# Revit family: Systemtrenner Nachfüll 0305
name_source: partatom
category: Rohrzubehör
units: mm (PartAtom-declared; Revit-internal decimal feet)

## family parameters
Arbeitsebenenbasiert = Nein
Beim Laden mit Abzugskörper schneiden = Nein
Bemaßung runder Anschluss = Durchmesser verwenden
Gemeinsam genutzt = Nein
Immer vertikal = Ja
OmniClass-Nummer = 23.65.55.14
OmniClass-Titel = Valves for Liquid Services
Teiletyp = Unterbricht

## types (1)
- Systemtrenner Nachfüll 0305
    Anwendung = Systemtrenner haben gemäß EN 1717 die Aufgabe ein Rückdrücken, Rückfließen oder Rücksaugen von verschmutztem Wasser in das Trinkwassernetz zu verhindern.
Der Einsatzbereich ist überall dort wo eine Verbindung zwischen dem Trinkwassernetz und Nutzwasser durch feste oder flexible Leitungen hergestellt wird.
Bevorzugte Anwendungsgebiete sind Enthärtungs-, Entsäuerungs- und Entkarbonisierungsanlagen.
Außerdem können die Systemtrenner in Desinfektionsanlagen oder vor chemischen Reinigungsapparaten eingesetzt werden um das Rückfließen von chemisch belastetem Wasser zu verhindern.
    Ausgangsdruck (regelbar) = 0.5-3 bar
    D02 = 15.2 mm
    D03 = 14.4 mm  [stored 0.0472441 ft]
    D04 = 12.9 mm
    D05 = 10.6 mm  [stored 0.0347769 ft]
    D06 = 16 mm  [stored 0.0524934 ft]
    D07 = 22 mm  [stored 0.0721785 ft]
    D08 = 18 mm  [stored 0.0590551 ft]
    D09 = 13.5 mm
    D10 = 16.3 mm  [stored 0.0534777 ft]
    D11 = 23.7 mm  [stored 0.0777559 ft]
    D12 = 22.8 mm  [stored 0.0748031 ft]
    D13 = 19.2 mm
    D14 = 14.2 mm  [stored 0.0465879 ft]
    D15 = 12.2 mm
    D16 = 66.7 mm
    D17 = 66.5 mm
    D18 = 92.3 mm
    Dichtungen = EPDM entsprechend KTW
    Einbaulage = waagerecht
    Gehäuse = Messing, CW617N
    Hersteller = HERZ Armaturen Ges.m.b.H.
    Hinweis = Gemäß Art 33 der REACH-Verordnung (EG Nr. 1907/2006) sind wir verpflichtet, darauf hinzuweisen, dass der Stoff Blei auf der SVHC-Liste geführt wird und dass alle aus Messing bestehenden Bauteile, die in unseren Erzeugnissen verarbeitet sind, mehr als 0,1 % (w/w) Blei (CAS: 7439-92-1 / EINECS: 231-100-4) enthalten.
Da Blei als Legierungsbestandteil fest gebunden ist, sind keine Expositionen zu erwarten und daher sind keine zusätzlichen Angaben zur sicheren Verwendung notwendig.
    L03 = 13 mm
    L04 = 10 mm  [stored 0.0328084 ft]
    L05 = 4.8 mm  [stored 0.015748 ft]
    L08 = 15.5 mm
    L09 = 26.2 mm
    L10 = 23.3 mm
    L11 = 4 mm  [stored 0.0131234 ft]
    L12 = 4.8 mm  [stored 0.015748 ft]
    L13 = 8.7 mm
    L14 = 30 mm  [stored 0.0984252 ft]
    L15 = 18.8 mm
    L16 = 70.5 mm
    L17 = 6.5 mm
    L18 = 8.7 mm
    L19 = 36.7 mm
    L20 = 12 mm  [stored 0.0393701 ft]
    L21 = 11 mm  [stored 0.0360892 ft]
    L22 = 22 mm  [stored 0.0721785 ft]
    L23 = 34 mm  [stored 0.111549 ft]
    L24 = 10.1 mm
    L25 = 28.6 mm
    L26 = 48.5 mm
    L27 = 44.5 mm
    L28 = 85.3 mm
    L29 = 28.8 mm  [stored 0.0944882 ft]
    Max. Betriebsdruck = 1000000.0 Pa
    Max. Betriebstemperatur = 65 °C
    Max. Betriebstemperatur (Kurzzeitig) = 85 °C
    Medium = Wasser
    R01 = 8 mm  [stored 0.0262467 ft]
    R02 = 7 mm  [stored 0.0229659 ft]
    R03 = 8.5 mm  [stored 0.0278871 ft]
    R04 = 7.5 mm  [stored 0.0246063 ft]
    R05 = 6.5 mm
    R06 = 7.3 mm
    R07 = 31 mm  [stored 0.101706 ft]
    R08 = 8.5 mm  [stored 0.0278871 ft]
    S03 = 40 mm
    S04 = 20 mm
    S05 = 8 mm  [stored 0.0262467 ft]
    S06 = 27 mm
    S07 = 75 mm
    S08 = 65 mm
    SCTWCODE = 04;12;02
    SCTWSEQ = AW;SBT_TYP_AW="104";2
    SC_NennweiteBerechnet = 0
    URL = www.herz-armaturen.at
    Voreingestellter Druck (werkseitig) = 150000.0 Pa
    Vorgabe-Ansicht = 0 mm  [stored 0 ft]
    W01 = 45.00°
    W02 = 80.00°

note: [stored X ft] marks values corroborated as IEEE doubles in the binary element streams (Revit-internal decimal feet)
